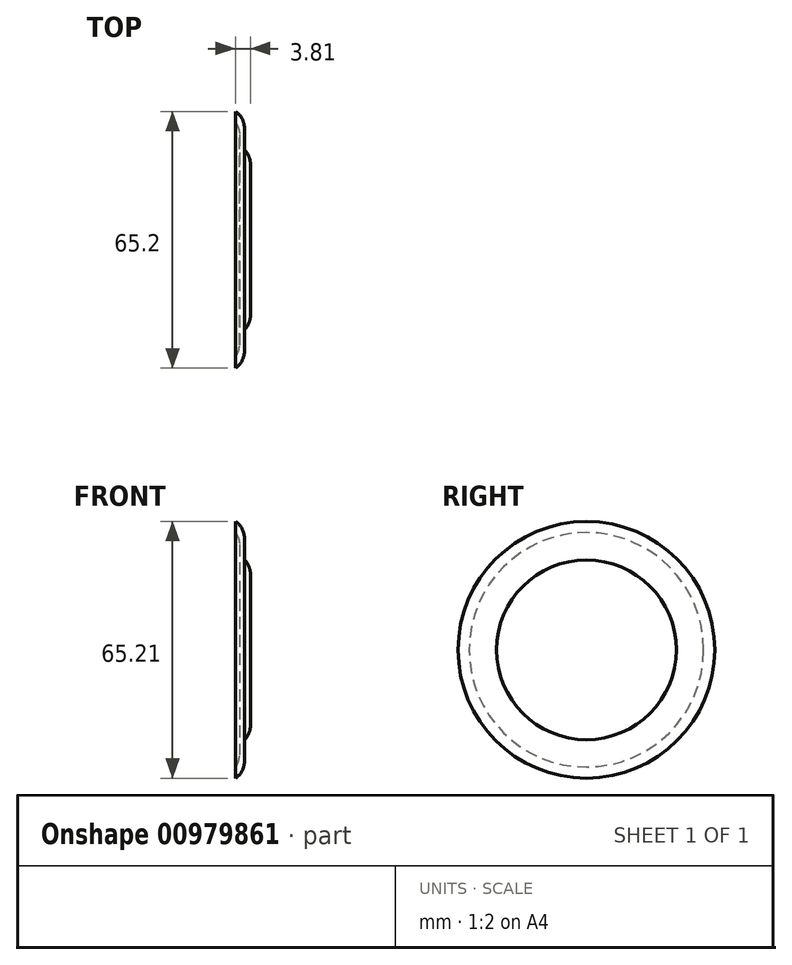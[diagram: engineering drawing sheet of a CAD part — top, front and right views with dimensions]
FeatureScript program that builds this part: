
annotation { "Feature Type Name" : "Feature", "Feature Type Description" : "" }
export const myFeature = defineFeature(function(context is Context, id is Id, definition is map)
    precondition{}
    {
        {
            var Q0;
            Q0=qCreatedBy(makeId("Right.planeOp"),FACE);
            var sketch = newSketch(context, id + "F0", { "sketchPlane" : qUnion([Q0])});
            skCircle(sketch, "E0", {"center": v(-40.86, 32.9) * mm, "radius": 32.6 * mm});
            skSolve(sketch);
        }
        {
            var Q0;
            Q0=makeQuery(id+"F0.imprint","IMPRINT",FACE,{"disambiguationData":[TD([[makeQuery(id+"F0.imprint","IMPRINT",EDGE,{"derivedFrom":sQuery(id+"F0.wireOp",EDGE,"E0")}),1.0]])]});
            extrude(context, id + "F1", {"entities" : qUnion([Q0]), "depth" : 2.3 * mm, "offsetDistance" : 25.4 * mm});
        }
        {
            var Q0;
            Q0=makeQuery(id+"F1.opExtrude","CAP_FACE",FACE,{"disambiguationData":[OSD([sQuery(id+"F0.wireOp",EDGE,"E0")])],"isStart":false});
            var sketch = newSketch(context, id + "F2", { "sketchPlane" : qUnion([Q0])});
            skCircle(sketch, "E1", {"center": v(-40.86, 32.9) * mm, "radius": 22.83 * mm});
            skSolve(sketch);
        }
        {
            var Q0;
            Q0=makeQuery(id+"F2.imprint","IMPRINT",FACE,{"disambiguationData":[TD([[makeQuery(id+"F2.imprint","IMPRINT",EDGE,{"derivedFrom":sQuery(id+"F2.wireOp",EDGE,"E1")}),1.0]])]});
            extrude(context, id + "F3", {"entities" : qUnion([Q0]), "operationType" : NewBodyOperationType.ADD, "depth" : 1.52 * mm, "offsetDistance" : 25.4 * mm});
        }
        {
            var Q0;
            Q0=makeQuery(id+"F3.opExtrude","CAP_EDGE",EDGE,{"disambiguationData":[OSD([sQuery(id+"F2.wireOp",EDGE,"E1")])],"isStart":false});
            fillet(context, id + "F4", {"entities" : qUnion([Q0]), "radius" : 5.08 * mm, "tangentPropagation" : true, "allowEdgeOverflow" : false});
        }
        {
            var Q0;
            Q0=makeQuery(id+"F1.opExtrude","CAP_EDGE",EDGE,{"disambiguationData":[OSD([sQuery(id+"F0.wireOp",EDGE,"E0")])],"isStart":false});
            fillet(context, id + "F5", {"entities" : qUnion([Q0]), "radius" : 5.08 * mm, "tangentPropagation" : true, "allowEdgeOverflow" : false});
        }
        {
            var Q0;
            Q0=makeQuery(id+"F1.opExtrude","CAP_FACE",FACE,{"disambiguationData":[OSD([sQuery(id+"F0.wireOp",EDGE,"E0")])],"isStart":true});
            var sketch = newSketch(context, id + "F6", { "sketchPlane" : qUnion([Q0])});
            skCircle(sketch, "E2", {"center": v(40.86, 32.9) * mm, "radius": 29.79 * mm});
            skSolve(sketch);
        }
        {
            var Q0;
            Q0=makeQuery(id+"F6.imprint","IMPRINT",FACE,{"disambiguationData":[TD([[makeQuery(id+"F6.imprint","IMPRINT",EDGE,{"derivedFrom":sQuery(id+"F6.wireOp",EDGE,"E2")}),1.0]])]});
            extrude(context, id + "F7", {"entities" : qUnion([Q0]), "operationType" : NewBodyOperationType.REMOVE, "oppositeDirection" : true, "depth" : 1.02 * mm, "offsetDistance" : 25.4 * mm});
        }
        {
            var Q0;
            Q0=makeQuery(id+"F7.boolean.opBoolean","COPY",EDGE,{"derivedFrom":makeQuery(id+"F7.opExtrude","CAP_EDGE",EDGE,{"disambiguationData":[OSD([sQuery(id+"F6.wireOp",EDGE,"E2")])],"isStart":false})});
            fillet(context, id + "F8", {"entities" : qUnion([Q0]), "radius" : 5.08 * mm, "tangentPropagation" : true, "allowEdgeOverflow" : false});
        }
    });
